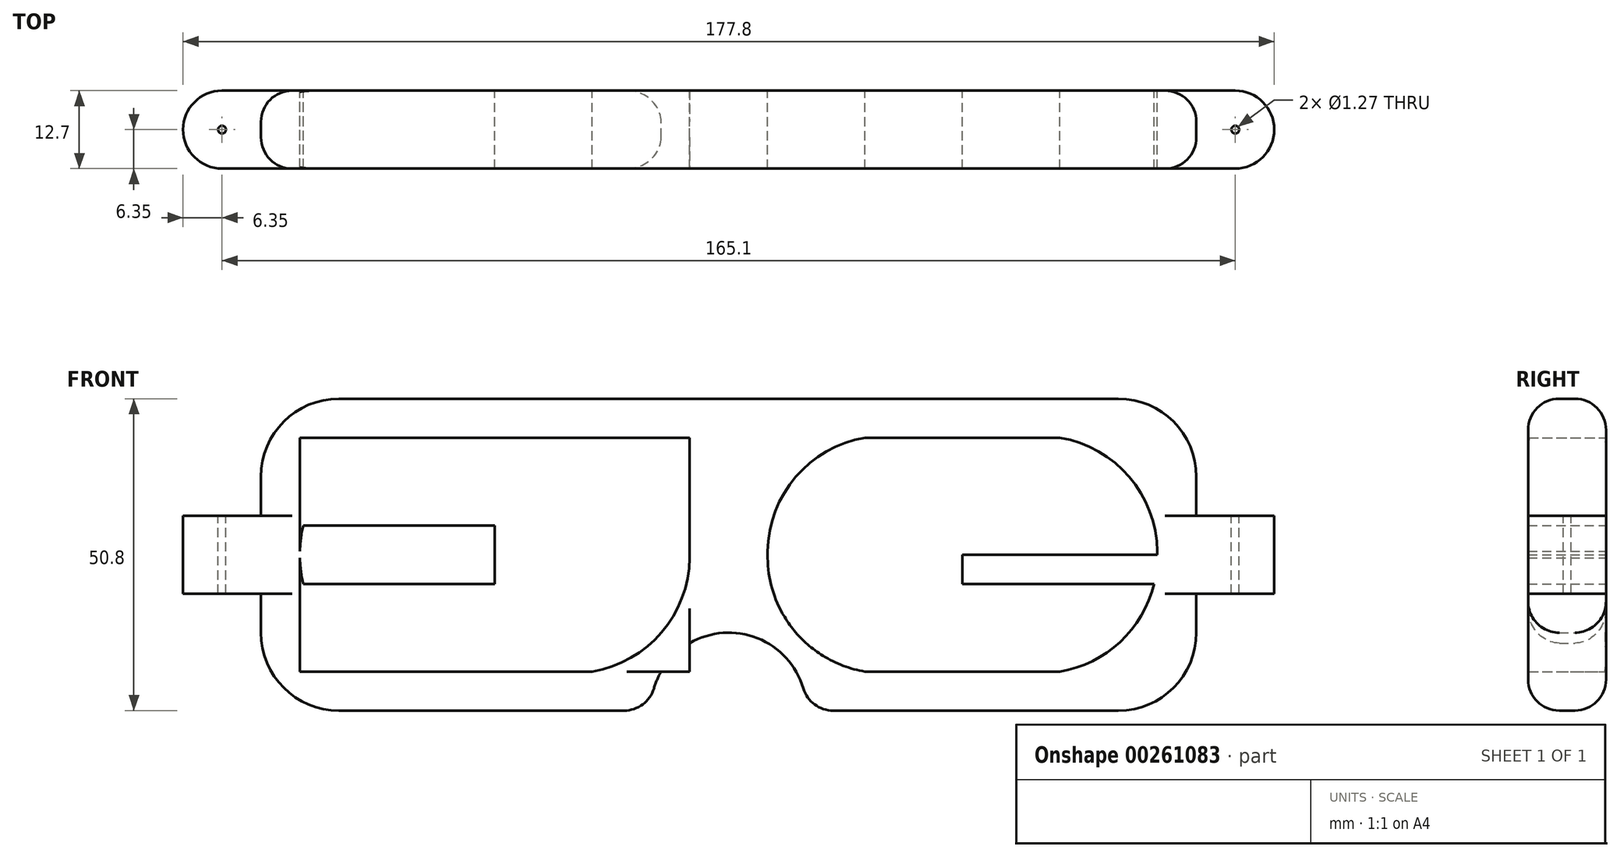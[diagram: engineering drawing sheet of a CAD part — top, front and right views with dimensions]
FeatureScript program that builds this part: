
annotation { "Feature Type Name" : "Feature", "Feature Type Description" : "" }
export const myFeature = defineFeature(function(context is Context, id is Id, definition is map)
    precondition{}
    {
        {
            var Q0;
            Q0=qCreatedBy(makeId("Front.planeOp"),FACE);
            var sketch = newSketch(context, id + "F0", { "sketchPlane" : qUnion([Q0])});
            skLineSegment(sketch, "E0.bottom", {"start": v(76.2, -25.4) * mm, "end": v(-76.2, -25.4) * mm});
            skLineSegment(sketch, "E0.top", {"start": v(76.2, 25.4) * mm, "end": v(-76.2, 25.4) * mm});
            skLineSegment(sketch, "E0.left", {"start": v(76.2, -25.4) * mm, "end": v(76.2, 25.4) * mm});
            skLineSegment(sketch, "E0.right", {"start": v(-76.2, -25.4) * mm, "end": v(-76.2, 25.4) * mm});
            skPoint(sketch, "E0.middle", {"position": v(0, 0) * mm});
            skLineSegment(sketch, "E1", {"start": v(-76.2, 0) * mm, "end": v(0, 0) * mm});
            skLineSegment(sketch, "E2", {"start": v(0, 0) * mm, "end": v(76.2, 0) * mm});
            skLineSegment(sketch, "E3.bottom", {"start": v(-6.35, -19.05) * mm, "end": v(-69.85, -19.05) * mm});
            skLineSegment(sketch, "E3.top", {"start": v(-6.35, 19.05) * mm, "end": v(-69.85, 19.05) * mm});
            skLineSegment(sketch, "E3.left", {"start": v(-6.35, -19.05) * mm, "end": v(-6.35, 19.05) * mm});
            skLineSegment(sketch, "E3.right", {"start": v(-69.85, -19.05) * mm, "end": v(-69.85, 19.05) * mm});
            skPoint(sketch, "E3.middle", {"position": v(-38.1, 0) * mm});
            skLineSegment(sketch, "E4", {"start": v(-38.1, 19.05) * mm, "end": v(-6.35, 19.05) * mm});
            skLineSegment(sketch, "E5", {"start": v(-38.1, 19.05) * mm, "end": v(-69.85, 19.05) * mm});
            skArc(sketch, "E6", {"start": v(-6.35, 0) * mm, "mid": v(-10.76, 12.46) * mm, "end": v(-22.22, 19.05) * mm});
            skArc(sketch, "E7", {"start": v(-53.98, 19.05) * mm, "mid": v(-65.44, 12.46) * mm, "end": v(-69.85, 0) * mm});
            skLineSegment(sketch, "E8", {"start": v(-38.1, -19.05) * mm, "end": v(-69.85, -19.05) * mm});
            skLineSegment(sketch, "E9", {"start": v(-38.1, -19.05) * mm, "end": v(-6.35, -19.05) * mm});
            skArc(sketch, "E10", {"start": v(-69.85, 0) * mm, "mid": v(-65.44, -12.46) * mm, "end": v(-53.97, -19.05) * mm});
            skArc(sketch, "E11", {"start": v(-22.23, -19.05) * mm, "mid": v(-10.76, -12.46) * mm, "end": v(-6.35, 0) * mm});
            skLineSegment(sketch, "E12.bottom", {"start": v(69.85, -19.05) * mm, "end": v(6.35, -19.05) * mm});
            skLineSegment(sketch, "E12.top", {"start": v(69.85, 19.05) * mm, "end": v(6.35, 19.05) * mm});
            skLineSegment(sketch, "E12.left", {"start": v(69.85, -19.05) * mm, "end": v(69.85, 19.05) * mm});
            skLineSegment(sketch, "E12.right", {"start": v(6.35, -19.05) * mm, "end": v(6.35, 19.05) * mm});
            skPoint(sketch, "E12.middle", {"position": v(38.1, 0) * mm});
            skArc(sketch, "E13", {"start": v(22.22, 19.05) * mm, "mid": v(10.76, 12.46) * mm, "end": v(6.35, 0) * mm});
            skArc(sketch, "E14", {"start": v(6.35, 0) * mm, "mid": v(10.76, -12.46) * mm, "end": v(22.22, -19.05) * mm});
            skArc(sketch, "E15", {"start": v(53.98, -19.05) * mm, "mid": v(65.44, -12.46) * mm, "end": v(69.85, 0) * mm});
            skArc(sketch, "E16", {"start": v(69.85, 0) * mm, "mid": v(65.44, 12.46) * mm, "end": v(53.98, 19.05) * mm});
            skLineSegment(sketch, "E17", {"start": v(38.1, 19.05) * mm, "end": v(38.1, -19.05) * mm});
            skLineSegment(sketch, "E18", {"start": v(38.1, 19.05) * mm, "end": v(38.1, 0) * mm});
            skLineSegment(sketch, "E19", {"start": v(38.1, 19.05) * mm, "end": v(38.1, 9.53) * mm});
            skLineSegment(sketch, "E20", {"start": v(38.1, 19.05) * mm, "end": v(38.1, 14.29) * mm});
            skLineSegment(sketch, "E21", {"start": v(38.1, 9.53) * mm, "end": v(38.1, 0) * mm});
            skLineSegment(sketch, "E22", {"start": v(38.1, 9.53) * mm, "end": v(38.1, 4.76) * mm});
            skLineSegment(sketch, "E23", {"start": v(38.1, 0) * mm, "end": v(38.1, -19.05) * mm});
            skLineSegment(sketch, "E24", {"start": v(38.1, 0) * mm, "end": v(38.1, -9.53) * mm});
            skLineSegment(sketch, "E25", {"start": v(38.1, 0) * mm, "end": v(38.1, -4.76) * mm});
            skLineSegment(sketch, "E26", {"start": v(38.1, -9.53) * mm, "end": v(38.1, -19.05) * mm});
            skLineSegment(sketch, "E27", {"start": v(38.1, -9.53) * mm, "end": v(38.1, -14.29) * mm});
            skLineSegment(sketch, "E28", {"start": v(-38.1, 19.05) * mm, "end": v(-38.1, -19.05) * mm});
            skLineSegment(sketch, "E29", {"start": v(-38.1, 19.05) * mm, "end": v(-38.1, 0) * mm});
            skLineSegment(sketch, "E30", {"start": v(-38.1, 19.05) * mm, "end": v(-38.1, 9.52) * mm});
            skLineSegment(sketch, "E31", {"start": v(-38.1, 19.05) * mm, "end": v(-38.1, 14.29) * mm});
            skLineSegment(sketch, "E32", {"start": v(-38.1, 9.52) * mm, "end": v(-38.1, 0) * mm});
            skLineSegment(sketch, "E33", {"start": v(-38.1, 9.52) * mm, "end": v(-38.1, 4.76) * mm});
            skLineSegment(sketch, "E34", {"start": v(-38.1, 0) * mm, "end": v(-38.1, -19.05) * mm});
            skLineSegment(sketch, "E35", {"start": v(-38.1, 0) * mm, "end": v(-38.1, -9.53) * mm});
            skLineSegment(sketch, "E36", {"start": v(-38.1, 0) * mm, "end": v(-38.1, -4.76) * mm});
            skLineSegment(sketch, "E37", {"start": v(-38.1, -9.53) * mm, "end": v(-38.1, -19.05) * mm});
            skLineSegment(sketch, "E38", {"start": v(-38.1, -9.53) * mm, "end": v(-38.1, -14.29) * mm});
            skLineSegment(sketch, "E39", {"start": v(38.1, 14.29) * mm, "end": v(63.7, 14.29) * mm});
            skLineSegment(sketch, "E40", {"start": v(38.1, 14.29) * mm, "end": v(12.5, 14.29) * mm});
            skLineSegment(sketch, "E41", {"start": v(38.1, 9.53) * mm, "end": v(67.45, 9.53) * mm});
            skLineSegment(sketch, "E42", {"start": v(38.1, 9.53) * mm, "end": v(8.75, 9.53) * mm});
            skLineSegment(sketch, "E43", {"start": v(38.1, 4.76) * mm, "end": v(69.31, 4.76) * mm});
            skLineSegment(sketch, "E44", {"start": v(38.1, 4.76) * mm, "end": v(6.89, 4.76) * mm});
            skLineSegment(sketch, "E45", {"start": v(38.1, 0) * mm, "end": v(69.85, 0) * mm});
            skLineSegment(sketch, "E46", {"start": v(38.1, 0) * mm, "end": v(6.35, 0) * mm});
            skLineSegment(sketch, "E47", {"start": v(38.1, -4.76) * mm, "end": v(69.31, -4.76) * mm});
            skLineSegment(sketch, "E48", {"start": v(38.1, -4.76) * mm, "end": v(6.89, -4.76) * mm});
            skLineSegment(sketch, "E49", {"start": v(38.1, -9.53) * mm, "end": v(67.45, -9.53) * mm});
            skLineSegment(sketch, "E50", {"start": v(38.1, -9.53) * mm, "end": v(8.75, -9.53) * mm});
            skLineSegment(sketch, "E51", {"start": v(38.1, -14.29) * mm, "end": v(63.7, -14.29) * mm});
            skLineSegment(sketch, "E52", {"start": v(38.1, -14.29) * mm, "end": v(12.5, -14.29) * mm});
            skLineSegment(sketch, "E53", {"start": v(-38.1, 14.29) * mm, "end": v(-12.5, 14.29) * mm});
            skLineSegment(sketch, "E54", {"start": v(-38.1, 14.29) * mm, "end": v(-63.7, 14.29) * mm});
            skLineSegment(sketch, "E55", {"start": v(-38.1, 9.52) * mm, "end": v(-8.75, 9.52) * mm});
            skLineSegment(sketch, "E56", {"start": v(-38.1, 9.52) * mm, "end": v(-67.45, 9.52) * mm});
            skLineSegment(sketch, "E57", {"start": v(-38.1, 4.76) * mm, "end": v(-6.89, 4.76) * mm});
            skLineSegment(sketch, "E58", {"start": v(-38.1, 4.76) * mm, "end": v(-69.31, 4.76) * mm});
            skLineSegment(sketch, "E59", {"start": v(-38.1, 0) * mm, "end": v(-6.35, 0) * mm});
            skLineSegment(sketch, "E60", {"start": v(-38.1, 0) * mm, "end": v(-69.85, 0) * mm});
            skLineSegment(sketch, "E61", {"start": v(-38.1, -4.76) * mm, "end": v(-6.89, -4.76) * mm});
            skLineSegment(sketch, "E62", {"start": v(-38.1, -4.76) * mm, "end": v(-69.31, -4.76) * mm});
            skLineSegment(sketch, "E63", {"start": v(-38.1, -9.53) * mm, "end": v(-8.75, -9.53) * mm});
            skLineSegment(sketch, "E64", {"start": v(-38.1, -9.53) * mm, "end": v(-67.45, -9.53) * mm});
            skLineSegment(sketch, "E65", {"start": v(-38.1, -14.29) * mm, "end": v(-12.5, -14.29) * mm});
            skLineSegment(sketch, "E66", {"start": v(-38.1, -14.29) * mm, "end": v(-63.7, -14.29) * mm});
            skLineSegment(sketch, "E67", {"start": v(0, -25.4) * mm, "end": v(0, -12.7) * mm});
            skCircle(sketch, "E68", {"center": v(0, -25.4) * mm, "radius": 12.7 * mm});
            skLineSegment(sketch, "E69", {"start": v(-76.2, 0) * mm, "end": v(-76.2, 25.4) * mm});
            skLineSegment(sketch, "E70", {"start": v(-76.2, 0) * mm, "end": v(-76.2, 6.35) * mm});
            skLineSegment(sketch, "E71", {"start": v(-76.2, 0) * mm, "end": v(-76.2, -6.35) * mm});
            skLineSegment(sketch, "E72.bottom", {"start": v(-76.2, 6.35) * mm, "end": v(-88.9, 6.35) * mm});
            skLineSegment(sketch, "E72.top", {"start": v(-76.2, -6.35) * mm, "end": v(-88.9, -6.35) * mm});
            skLineSegment(sketch, "E72.left", {"start": v(-76.2, 6.35) * mm, "end": v(-76.2, -6.35) * mm});
            skLineSegment(sketch, "E72.right", {"start": v(-88.9, 6.35) * mm, "end": v(-88.9, -6.35) * mm});
            skLineSegment(sketch, "E73", {"start": v(76.2, 25.4) * mm, "end": v(76.2, 0) * mm});
            skLineSegment(sketch, "E74", {"start": v(76.2, 0) * mm, "end": v(76.2, 6.35) * mm});
            skLineSegment(sketch, "E75.bottom", {"start": v(76.2, 6.35) * mm, "end": v(88.9, 6.35) * mm});
            skLineSegment(sketch, "E75.top", {"start": v(76.2, -6.35) * mm, "end": v(88.9, -6.35) * mm});
            skLineSegment(sketch, "E75.left", {"start": v(76.2, 6.35) * mm, "end": v(76.2, -6.35) * mm});
            skLineSegment(sketch, "E75.right", {"start": v(88.9, 6.35) * mm, "end": v(88.9, -6.35) * mm});
            skLineSegment(sketch, "E76", {"start": v(88.9, 6.35) * mm, "end": v(76.2, -6.35) * mm});
            skPoint(sketch, "E77", {"position": v(82.55, 0) * mm});
            skSolve(sketch);
        }
        {
            var Q0;
            Q0=makeQuery(id+"F0.imprint","IMPRINT",FACE,{"disambiguationData":[TD([[makeQuery(id+"F0.imprint","IMPRINT",EDGE,{"derivedFrom":sQuery(id+"F0.wireOp",EDGE,"E22")}),1.0]])]});
            var Q1;
            Q1=makeQuery(id+"F0.imprint","IMPRINT",FACE,{"disambiguationData":[TD([[makeQuery(id+"F0.imprint","IMPRINT",EDGE,{"derivedFrom":sQuery(id+"F0.wireOp",EDGE,"E0.top")}),1.0]])]});
            var Q2;
            {var subQ2=sQuery(id+"F0.wireOp",EDGE,"E3.right");var subQ5=sQuery(id+"F0.wireOp",EDGE,"E8");var subQ6=makeQuery(id+"F0.imprint","INTERSECT",VERTEX,{"derivedFrom":[subQ2,subQ5]});Q2=makeQuery(id+"F0.imprint","IMPRINT",FACE,{"disambiguationData":[TD([[makeQuery(id+"F0.imprint","IMPRINT",EDGE,{"disambiguationData":[TD([[subQ6,-1.0]])],"derivedFrom":subQ2}),-1.0]])]});}
            var Q3;
            {var subQ3=sQuery(id+"F0.wireOp",EDGE,"E5");var subQ4=sQuery(id+"F0.wireOp",EDGE,"E3.right");var subQ5=makeQuery(id+"F0.imprint","INTERSECT",VERTEX,{"derivedFrom":[subQ4,subQ3]});Q3=makeQuery(id+"F0.imprint","IMPRINT",FACE,{"disambiguationData":[TD([[makeQuery(id+"F0.imprint","IMPRINT",EDGE,{"disambiguationData":[TD([[subQ5,1.0]])],"derivedFrom":subQ4}),-1.0]])]});}
            var Q4;
            Q4=makeQuery(id+"F0.imprint","IMPRINT",FACE,{"disambiguationData":[TD([[makeQuery(id+"F0.imprint","IMPRINT",EDGE,{"derivedFrom":sQuery(id+"F0.wireOp",EDGE,"E22")}),-1.0]])]});
            var Q5;
            Q5=makeQuery(id+"F0.imprint","IMPRINT",FACE,{"disambiguationData":[TD([[makeQuery(id+"F0.imprint","IMPRINT",EDGE,{"derivedFrom":sQuery(id+"F0.wireOp",EDGE,"E36")}),-1.0]])]});
            var Q6;
            {var subQ3=sQuery(id+"F0.wireOp",EDGE,"q7rADGaM-sFZv-4VIx-AgKo-KgdgV1lt6V0s");var subQ4=sQuery(id+"F0.wireOp",EDGE,"E12.left");var subQ5=makeQuery(id+"F0.imprint","INTERSECT",VERTEX,{"derivedFrom":[subQ4,subQ3]});Q6=makeQuery(id+"F0.imprint","IMPRINT",FACE,{"disambiguationData":[TD([[makeQuery(id+"F0.imprint","IMPRINT",EDGE,{"disambiguationData":[TD([[subQ5,-1.0]])],"derivedFrom":subQ4}),1.0]])]});}
            var Q7;
            {var subQ6=sQuery(id+"F0.wireOp",EDGE,"E68");var subQ10=sQuery(id+"F0.wireOp",EDGE,"E3.left");var subQ13=makeQuery(id+"F0.imprint","INTERSECT",VERTEX,{"derivedFrom":[subQ10,subQ6]});Q7=makeQuery(id+"F0.imprint","IMPRINT",FACE,{"disambiguationData":[TD([[makeQuery(id+"F0.imprint","IMPRINT",EDGE,{"disambiguationData":[TD([[subQ13,-1.0]])],"derivedFrom":subQ10}),-1.0]])]});}
            var Q8;
            {var subQ5=sQuery(id+"F0.wireOp",EDGE,"E68");var subQ7=sQuery(id+"F0.wireOp",EDGE,"E3.left");var subQ8=makeQuery(id+"F0.imprint","INTERSECT",VERTEX,{"derivedFrom":[subQ7,subQ5]});Q8=makeQuery(id+"F0.imprint","IMPRINT",FACE,{"disambiguationData":[TD([[makeQuery(id+"F0.imprint","IMPRINT",EDGE,{"disambiguationData":[TD([[subQ8,-1.0]])],"derivedFrom":subQ7}),1.0]])]});}
            var Q9;
            Q9=makeQuery(id+"F0.imprint","IMPRINT",FACE,{"disambiguationData":[TD([[makeQuery(id+"F0.imprint","IMPRINT",EDGE,{"derivedFrom":sQuery(id+"F0.wireOp",EDGE,"E38")}),-1.0]])]});
            var Q10;
            Q10=makeQuery(id+"F0.imprint","IMPRINT",FACE,{"disambiguationData":[TD([[makeQuery(id+"F0.imprint","IMPRINT",EDGE,{"derivedFrom":sQuery(id+"F0.wireOp",EDGE,"E33")}),1.0]])]});
            var Q11;
            {var subQ0=sQuery(id+"F0.wireOp",EDGE,"E31");Q11=makeQuery(id+"F0.imprint","IMPRINT",FACE,{"disambiguationData":[TD([[makeQuery(id+"F0.imprint","IMPRINT",EDGE,{"derivedFrom":subQ0}),1.0]])]});}
            var Q12;
            {var subQ0=sQuery(id+"F0.wireOp",EDGE,"E31");Q12=makeQuery(id+"F0.imprint","IMPRINT",FACE,{"disambiguationData":[TD([[makeQuery(id+"F0.imprint","IMPRINT",EDGE,{"derivedFrom":subQ0}),-1.0]])]});}
            var Q13;
            Q13=makeQuery(id+"F0.imprint","IMPRINT",FACE,{"disambiguationData":[TD([[makeQuery(id+"F0.imprint","IMPRINT",EDGE,{"derivedFrom":sQuery(id+"F0.wireOp",EDGE,"E27")}),1.0]])]});
            var Q14;
            {var subQ3=sQuery(id+"F0.wireOp",EDGE,"E72.bottom");Q14=makeQuery(id+"F0.imprint","IMPRINT",FACE,{"disambiguationData":[TD([[makeQuery(id+"F0.imprint","IMPRINT",EDGE,{"derivedFrom":subQ3}),1.0]])]});}
            var Q15;
            {var subQ3=sQuery(id+"F0.wireOp",EDGE,"E75.bottom");Q15=makeQuery(id+"F0.imprint","IMPRINT",FACE,{"disambiguationData":[TD([[makeQuery(id+"F0.imprint","IMPRINT",EDGE,{"derivedFrom":subQ3}),-1.0]])]});}
            var Q16;
            {var subQ3=sQuery(id+"F0.wireOp",EDGE,"E68");var subQ7=sQuery(id+"F0.wireOp",EDGE,"E12.right");var subQ8=makeQuery(id+"F0.imprint","INTERSECT",VERTEX,{"derivedFrom":[subQ7,subQ3]});Q16=makeQuery(id+"F0.imprint","IMPRINT",FACE,{"disambiguationData":[TD([[makeQuery(id+"F0.imprint","IMPRINT",EDGE,{"disambiguationData":[TD([[subQ8,-1.0]])],"derivedFrom":subQ7}),-1.0]])]});}
            var Q17;
            Q17=makeQuery(id+"F0.imprint","IMPRINT",FACE,{"disambiguationData":[TD([[makeQuery(id+"F0.imprint","IMPRINT",EDGE,{"derivedFrom":sQuery(id+"F0.wireOp",EDGE,"E36")}),1.0]])]});
            var Q18;
            Q18=makeQuery(id+"F0.imprint","IMPRINT",FACE,{"disambiguationData":[TD([[makeQuery(id+"F0.imprint","IMPRINT",EDGE,{"derivedFrom":sQuery(id+"F0.wireOp",EDGE,"E38")}),1.0]])]});
            var Q19;
            {var subQ8=sQuery(id+"F0.wireOp",EDGE,"E0.left");Q19=makeQuery(id+"F0.imprint","IMPRINT",FACE,{"disambiguationData":[TD([[makeQuery(id+"F0.imprint","IMPRINT",EDGE,{"derivedFrom":subQ8}),1.0]])]});}
            var Q20;
            Q20=makeQuery(id+"F0.imprint","IMPRINT",FACE,{"disambiguationData":[TD([[makeQuery(id+"F0.imprint","IMPRINT",EDGE,{"derivedFrom":sQuery(id+"F0.wireOp",EDGE,"E33")}),-1.0]])]});
            var Q21;
            Q21=makeQuery(id+"F0.imprint","IMPRINT",FACE,{"disambiguationData":[TD([[makeQuery(id+"F0.imprint","IMPRINT",EDGE,{"derivedFrom":sQuery(id+"F0.wireOp",EDGE,"E25")}),-1.0]])]});
            var Q22;
            {var subQ0=sQuery(id+"F0.wireOp",EDGE,"E20");Q22=makeQuery(id+"F0.imprint","IMPRINT",FACE,{"disambiguationData":[TD([[makeQuery(id+"F0.imprint","IMPRINT",EDGE,{"derivedFrom":subQ0}),1.0]])]});}
            var Q23;
            Q23=makeQuery(id+"F0.imprint","IMPRINT",FACE,{"disambiguationData":[TD([[makeQuery(id+"F0.imprint","IMPRINT",EDGE,{"derivedFrom":sQuery(id+"F0.wireOp",EDGE,"E27")}),-1.0]])]});
            var Q24;
            {var subQ15=sQuery(id+"F0.wireOp",EDGE,"lpfGSqYw-B6LC-D4AK-ky7f-vD2tKFUR33Au");Q24=makeQuery(id+"F0.imprint","IMPRINT",FACE,{"disambiguationData":[TD([[makeQuery(id+"F0.imprint","IMPRINT",EDGE,{"derivedFrom":subQ15}),1.0]])]});}
            var Q25;
            {var subQ2=sQuery(id+"F0.wireOp",EDGE,"E3.left");var subQ5=sQuery(id+"F0.wireOp",EDGE,"E4");var subQ6=makeQuery(id+"F0.imprint","INTERSECT",VERTEX,{"derivedFrom":[subQ2,subQ5]});Q25=makeQuery(id+"F0.imprint","IMPRINT",FACE,{"disambiguationData":[TD([[makeQuery(id+"F0.imprint","IMPRINT",EDGE,{"disambiguationData":[TD([[subQ6,1.0]])],"derivedFrom":subQ2}),1.0]])]});}
            var Q26;
            {var subQ0=sQuery(id+"F0.wireOp",EDGE,"E20");Q26=makeQuery(id+"F0.imprint","IMPRINT",FACE,{"disambiguationData":[TD([[makeQuery(id+"F0.imprint","IMPRINT",EDGE,{"derivedFrom":subQ0}),-1.0]])]});}
            var Q27;
            Q27=makeQuery(id+"F0.imprint","IMPRINT",FACE,{"disambiguationData":[TD([[makeQuery(id+"F0.imprint","IMPRINT",EDGE,{"derivedFrom":sQuery(id+"F0.wireOp",EDGE,"E25")}),1.0]])]});
            var Q28;
            {var subQ0=sQuery(id+"F0.wireOp",EDGE,"E6");var subQ1=sQuery(id+"F0.wireOp",EDGE,"E3.left");var subQ3=makeQuery(id+"F0.imprint","INTERSECT",VERTEX,{"derivedFrom":[subQ1,subQ0]});Q28=makeQuery(id+"F0.imprint","IMPRINT",FACE,{"disambiguationData":[TD([[makeQuery(id+"F0.imprint","IMPRINT",EDGE,{"disambiguationData":[TD([[subQ3,1.0]])],"derivedFrom":subQ1}),-1.0]])]});}
            var Q29;
            {var subQ0=sQuery(id+"F0.wireOp",EDGE,"E10");var subQ1=sQuery(id+"F0.wireOp",EDGE,"E3.right");var subQ3=makeQuery(id+"F0.imprint","INTERSECT",VERTEX,{"derivedFrom":[subQ1,subQ0]});Q29=makeQuery(id+"F0.imprint","IMPRINT",FACE,{"disambiguationData":[TD([[makeQuery(id+"F0.imprint","IMPRINT",EDGE,{"disambiguationData":[TD([[subQ3,-1.0]])],"derivedFrom":subQ1}),1.0]])]});}
            var Q30;
            {var subQ0=sQuery(id+"F0.wireOp",EDGE,"E7");var subQ1=sQuery(id+"F0.wireOp",EDGE,"E3.right");var subQ3=makeQuery(id+"F0.imprint","INTERSECT",VERTEX,{"derivedFrom":[subQ1,subQ0]});Q30=makeQuery(id+"F0.imprint","IMPRINT",FACE,{"disambiguationData":[TD([[makeQuery(id+"F0.imprint","IMPRINT",EDGE,{"disambiguationData":[TD([[subQ3,1.0]])],"derivedFrom":subQ1}),1.0]])]});}
            var Q31;
            {var subQ0=sQuery(id+"F0.wireOp",EDGE,"E15");var subQ1=sQuery(id+"F0.wireOp",EDGE,"E12.left");var subQ3=makeQuery(id+"F0.imprint","INTERSECT",VERTEX,{"derivedFrom":[subQ1,subQ0]});Q31=makeQuery(id+"F0.imprint","IMPRINT",FACE,{"disambiguationData":[TD([[makeQuery(id+"F0.imprint","IMPRINT",EDGE,{"disambiguationData":[TD([[subQ3,-1.0]])],"derivedFrom":subQ1}),-1.0]])]});}
            var Q32;
            {var subQ0=sQuery(id+"F0.wireOp",EDGE,"E16");var subQ1=sQuery(id+"F0.wireOp",EDGE,"E12.left");var subQ3=makeQuery(id+"F0.imprint","INTERSECT",VERTEX,{"derivedFrom":[subQ1,subQ0]});Q32=makeQuery(id+"F0.imprint","IMPRINT",FACE,{"disambiguationData":[TD([[makeQuery(id+"F0.imprint","IMPRINT",EDGE,{"disambiguationData":[TD([[subQ3,1.0]])],"derivedFrom":subQ1}),-1.0]])]});}
            var Q33;
            {var subQ0=sQuery(id+"F0.wireOp",EDGE,"E14");var subQ1=sQuery(id+"F0.wireOp",EDGE,"E12.right");var subQ3=makeQuery(id+"F0.imprint","INTERSECT",VERTEX,{"derivedFrom":[subQ1,subQ0]});Q33=makeQuery(id+"F0.imprint","IMPRINT",FACE,{"disambiguationData":[TD([[makeQuery(id+"F0.imprint","IMPRINT",EDGE,{"disambiguationData":[TD([[subQ3,-1.0]])],"derivedFrom":subQ1}),1.0]])]});}
            var Q34;
            {var subQ0=sQuery(id+"F0.wireOp",EDGE,"E13");var subQ1=sQuery(id+"F0.wireOp",EDGE,"E12.right");var subQ3=makeQuery(id+"F0.imprint","INTERSECT",VERTEX,{"derivedFrom":[subQ1,subQ0]});Q34=makeQuery(id+"F0.imprint","IMPRINT",FACE,{"disambiguationData":[TD([[makeQuery(id+"F0.imprint","IMPRINT",EDGE,{"disambiguationData":[TD([[subQ3,1.0]])],"derivedFrom":subQ1}),1.0]])]});}
            var Q35;
            {var subQ0=sQuery(id+"F0.wireOp",EDGE,"E11");var subQ1=sQuery(id+"F0.wireOp",EDGE,"E3.left");var subQ3=makeQuery(id+"F0.imprint","INTERSECT",VERTEX,{"derivedFrom":[subQ1,subQ0]});Q35=makeQuery(id+"F0.imprint","IMPRINT",FACE,{"disambiguationData":[TD([[makeQuery(id+"F0.imprint","IMPRINT",EDGE,{"disambiguationData":[TD([[subQ3,-1.0]])],"derivedFrom":subQ1}),-1.0]])]});}
            var Q36;
            {var subQ15=sQuery(id+"F0.wireOp",EDGE,"E0.right");Q36=makeQuery(id+"F0.imprint","IMPRINT",FACE,{"disambiguationData":[TD([[makeQuery(id+"F0.imprint","IMPRINT",EDGE,{"derivedFrom":subQ15}),-1.0]])]});}
            var Q37;
            {var subQ3=sQuery(id+"F0.wireOp",EDGE,"E12.top");var subQ5=sQuery(id+"F0.wireOp",EDGE,"E12.right");var subQ6=makeQuery(id+"F0.imprint","INTERSECT",VERTEX,{"derivedFrom":[subQ3,subQ5]});Q37=makeQuery(id+"F0.imprint","IMPRINT",FACE,{"disambiguationData":[TD([[makeQuery(id+"F0.imprint","IMPRINT",EDGE,{"disambiguationData":[TD([[subQ6,1.0]])],"derivedFrom":subQ3}),1.0]])]});}
            var Q38;
            {var subQ0=sQuery(id+"F0.wireOp",EDGE,"E12.left");var subQ1=sQuery(id+"F0.wireOp",EDGE,"E12.top");var subQ2=makeQuery(id+"F0.imprint","INTERSECT",VERTEX,{"derivedFrom":[subQ1,subQ0]});Q38=makeQuery(id+"F0.imprint","IMPRINT",FACE,{"disambiguationData":[TD([[makeQuery(id+"F0.imprint","IMPRINT",EDGE,{"disambiguationData":[TD([[subQ2,-1.0]])],"derivedFrom":subQ1}),1.0]])]});}
            var Q39;
            {var subQ3=sQuery(id+"F0.wireOp",EDGE,"E12.bottom");var subQ5=sQuery(id+"F0.wireOp",EDGE,"E12.left");var subQ6=makeQuery(id+"F0.imprint","INTERSECT",VERTEX,{"derivedFrom":[subQ3,subQ5]});Q39=makeQuery(id+"F0.imprint","IMPRINT",FACE,{"disambiguationData":[TD([[makeQuery(id+"F0.imprint","IMPRINT",EDGE,{"disambiguationData":[TD([[subQ6,-1.0]])],"derivedFrom":subQ3}),-1.0]])]});}
            var Q40;
            Q40=makeQuery(id+"F0.imprint","IMPRINT",FACE,{"disambiguationData":[TD([[makeQuery(id+"F0.imprint","IMPRINT",EDGE,{"derivedFrom":sQuery(id+"F0.wireOp",EDGE,"E75.top")}),1.0]])]});
            extrude(context, id + "F1", {"entities" : qUnion([Q0, Q1, Q2, Q3, Q4, Q5, Q6, Q7, Q8, Q9, Q10, Q11, Q12, Q13, Q14, Q15, Q16, Q17, Q18, Q19, Q20, Q21, Q22, Q23, Q24, Q25, Q26, Q27, Q28, Q29, Q30, Q31, Q32, Q33, Q34, Q35, Q36, Q37, Q38, Q39, Q40]), "depth" : 12.7 * mm});
        }
        {
            var Q0;
            Q0=makeQuery(id+"F1.opExtrude","SWEPT_FACE",FACE,{"disambiguationData":[OSD([sQuery(id+"F0.wireOp",EDGE,"E72.bottom")])]});
            var sketch = newSketch(context, id + "F2", { "sketchPlane" : qUnion([Q0])});
            skLineSegment(sketch, "E78", {"start": v(-88.9, 0) * mm, "end": v(-76.2, -12.7) * mm});
            skCircle(sketch, "E79", {"center": v(-82.55, -6.35) * mm, "radius": 0.64 * mm});
            skSolve(sketch);
        }
        {
            var Q0;
            Q0=makeQuery(id+"F1.opExtrude","SWEPT_FACE",FACE,{"disambiguationData":[OSD([sQuery(id+"F0.wireOp",EDGE,"E75.bottom")])]});
            var sketch = newSketch(context, id + "F3", { "sketchPlane" : qUnion([Q0])});
            skLineSegment(sketch, "E80", {"start": v(76.2, 0) * mm, "end": v(88.9, -12.7) * mm});
            skCircle(sketch, "E81", {"center": v(82.55, -6.35) * mm, "radius": 0.64 * mm});
            skSolve(sketch);
        }
        {
            var Q0;
            {var subQ0=sQuery(id+"F2.wireOp",EDGE,"E79");var subQ1=sQuery(id+"F2.wireOp",EDGE,"E78");var subQ2=makeQuery(id+"F2.imprint","INTERSECT",VERTEX,{"disambiguationData":[OD(0.0)],"derivedFrom":[subQ1,subQ0]});Q0=makeQuery(id+"F2.imprint","IMPRINT",FACE,{"disambiguationData":[TD([[makeQuery(id+"F2.imprint","IMPRINT",EDGE,{"disambiguationData":[TD([[subQ2,-1.0]])],"derivedFrom":subQ1}),1.0]])]});}
            var Q1;
            {var subQ0=sQuery(id+"F2.wireOp",EDGE,"E79");var subQ1=sQuery(id+"F2.wireOp",EDGE,"E78");var subQ2=makeQuery(id+"F2.imprint","INTERSECT",VERTEX,{"disambiguationData":[OD(0.0)],"derivedFrom":[subQ1,subQ0]});Q1=makeQuery(id+"F2.imprint","IMPRINT",FACE,{"disambiguationData":[TD([[makeQuery(id+"F2.imprint","IMPRINT",EDGE,{"disambiguationData":[TD([[subQ2,-1.0]])],"derivedFrom":subQ1}),-1.0]])]});}
            extrude(context, id + "F4", {"entities" : qUnion([Q0, Q1]), "operationType" : NewBodyOperationType.REMOVE, "oppositeDirection" : true, "depth" : 12.7 * mm});
        }
        {
            var Q0;
            {var subQ0=sQuery(id+"F3.wireOp",EDGE,"E81");var subQ1=sQuery(id+"F3.wireOp",EDGE,"E80");var subQ2=makeQuery(id+"F3.imprint","INTERSECT",VERTEX,{"disambiguationData":[OD(0.0)],"derivedFrom":[subQ1,subQ0]});Q0=makeQuery(id+"F3.imprint","IMPRINT",FACE,{"disambiguationData":[TD([[makeQuery(id+"F3.imprint","IMPRINT",EDGE,{"disambiguationData":[TD([[subQ2,-1.0]])],"derivedFrom":subQ1}),1.0]])]});}
            var Q1;
            {var subQ0=sQuery(id+"F3.wireOp",EDGE,"E81");var subQ1=sQuery(id+"F3.wireOp",EDGE,"E80");var subQ2=makeQuery(id+"F3.imprint","INTERSECT",VERTEX,{"disambiguationData":[OD(0.0)],"derivedFrom":[subQ1,subQ0]});Q1=makeQuery(id+"F3.imprint","IMPRINT",FACE,{"disambiguationData":[TD([[makeQuery(id+"F3.imprint","IMPRINT",EDGE,{"disambiguationData":[TD([[subQ2,-1.0]])],"derivedFrom":subQ1}),-1.0]])]});}
            extrude(context, id + "F5", {"entities" : qUnion([Q0, Q1]), "operationType" : NewBodyOperationType.REMOVE, "oppositeDirection" : true, "depth" : 12.7 * mm});
        }
        {
            var Q0;
            Q0=makeQuery(id+"F1.opExtrude","CAP_EDGE",EDGE,{"disambiguationData":[OSD([sQuery(id+"F0.wireOp",EDGE,"E75.right")])],"isStart":true});
            var Q1;
            Q1=makeQuery(id+"F1.opExtrude","CAP_EDGE",EDGE,{"disambiguationData":[OSD([sQuery(id+"F0.wireOp",EDGE,"E75.right")])],"isStart":false});
            var Q2;
            Q2=makeQuery(id+"F1.opExtrude","CAP_EDGE",EDGE,{"disambiguationData":[OSD([sQuery(id+"F0.wireOp",EDGE,"E72.right")])],"isStart":false});
            var Q3;
            Q3=makeQuery(id+"F1.opExtrude","CAP_EDGE",EDGE,{"disambiguationData":[OSD([sQuery(id+"F0.wireOp",EDGE,"E72.right")])],"isStart":true});
            fillet(context, id + "F6", {"entities" : qUnion([Q0, Q1, Q2, Q3]), "radius" : 6.35 * mm, "tangentPropagation" : true, "allowEdgeOverflow" : false});
        }
        {
            var Q0;
            {var subQ0=sQuery(id+"F0.wireOp",EDGE,"E68");var subQ1=sQuery(id+"F0.wireOp",EDGE,"E0.bottom");Q0=makeQuery(id+"F1.opExtrude","SWEPT_EDGE",EDGE,{"disambiguationData":[OSD([subQ1,subQ0]),TDD([makeQuery(id+"F0.imprint","INTERSECT",VERTEX,{"disambiguationData":[OD(1.0)],"derivedFrom":[subQ1,subQ0]})])]});}
            var Q1;
            {var subQ0=sQuery(id+"F0.wireOp",EDGE,"E68");var subQ1=sQuery(id+"F0.wireOp",EDGE,"E0.bottom");Q1=makeQuery(id+"F1.opExtrude","SWEPT_EDGE",EDGE,{"disambiguationData":[OSD([subQ1,subQ0]),TDD([makeQuery(id+"F0.imprint","INTERSECT",VERTEX,{"disambiguationData":[OD(0.0)],"derivedFrom":[subQ1,subQ0]})])]});}
            fillet(context, id + "F7", {"entities" : qUnion([Q0, Q1]), "radius" : 5.08 * mm, "tangentPropagation" : true, "allowEdgeOverflow" : false});
        }
        {
            var Q0;
            Q0=makeQuery(id+"F1.opExtrude","SWEPT_EDGE",EDGE,{"disambiguationData":[OSD([sQuery(id+"F0.wireOp",EDGE,"E0.top"),sQuery(id+"F0.wireOp",EDGE,"E73")])]});
            var Q1;
            Q1=makeQuery(id+"F1.opExtrude","SWEPT_EDGE",EDGE,{"disambiguationData":[OSD([sQuery(id+"F0.wireOp",EDGE,"E0.bottom"),sQuery(id+"F0.wireOp",EDGE,"E0.left")])]});
            var Q2;
            Q2=makeQuery(id+"F1.opExtrude","SWEPT_EDGE",EDGE,{"disambiguationData":[OSD([sQuery(id+"F0.wireOp",EDGE,"E0.bottom"),sQuery(id+"F0.wireOp",EDGE,"E0.right")])]});
            var Q3;
            Q3=makeQuery(id+"F1.opExtrude","SWEPT_EDGE",EDGE,{"disambiguationData":[OSD([sQuery(id+"F0.wireOp",EDGE,"E0.top"),sQuery(id+"F0.wireOp",EDGE,"E69")])]});
            fillet(context, id + "F8", {"entities" : qUnion([Q0, Q1, Q2, Q3]), "radius" : 12.7 * mm, "tangentPropagation" : true, "allowEdgeOverflow" : false});
        }
        {
            var Q0;
            Q0=makeQuery(id+"F1.opExtrude","CAP_EDGE",EDGE,{"disambiguationData":[OSD([sQuery(id+"F0.wireOp",EDGE,"E68")])],"isStart":true});
            var Q1;
            Q1=makeQuery(id+"F1.opExtrude","CAP_EDGE",EDGE,{"disambiguationData":[OSD([sQuery(id+"F0.wireOp",EDGE,"E68")])],"isStart":false});
            var Q2;
            Q2=makeQuery(id+"F1.opExtrude","CAP_EDGE",EDGE,{"disambiguationData":[OSD([sQuery(id+"F0.wireOp",EDGE,"E0.top")])],"isStart":true});
            var Q3;
            Q3=makeQuery(id+"F1.opExtrude","CAP_EDGE",EDGE,{"disambiguationData":[OSD([sQuery(id+"F0.wireOp",EDGE,"E0.top")])],"isStart":false});
            fillet(context, id + "F9", {"entities" : qUnion([Q0, Q1, Q2, Q3]), "radius" : 5.08 * mm, "tangentPropagation" : true, "allowEdgeOverflow" : false});
        }
    });
